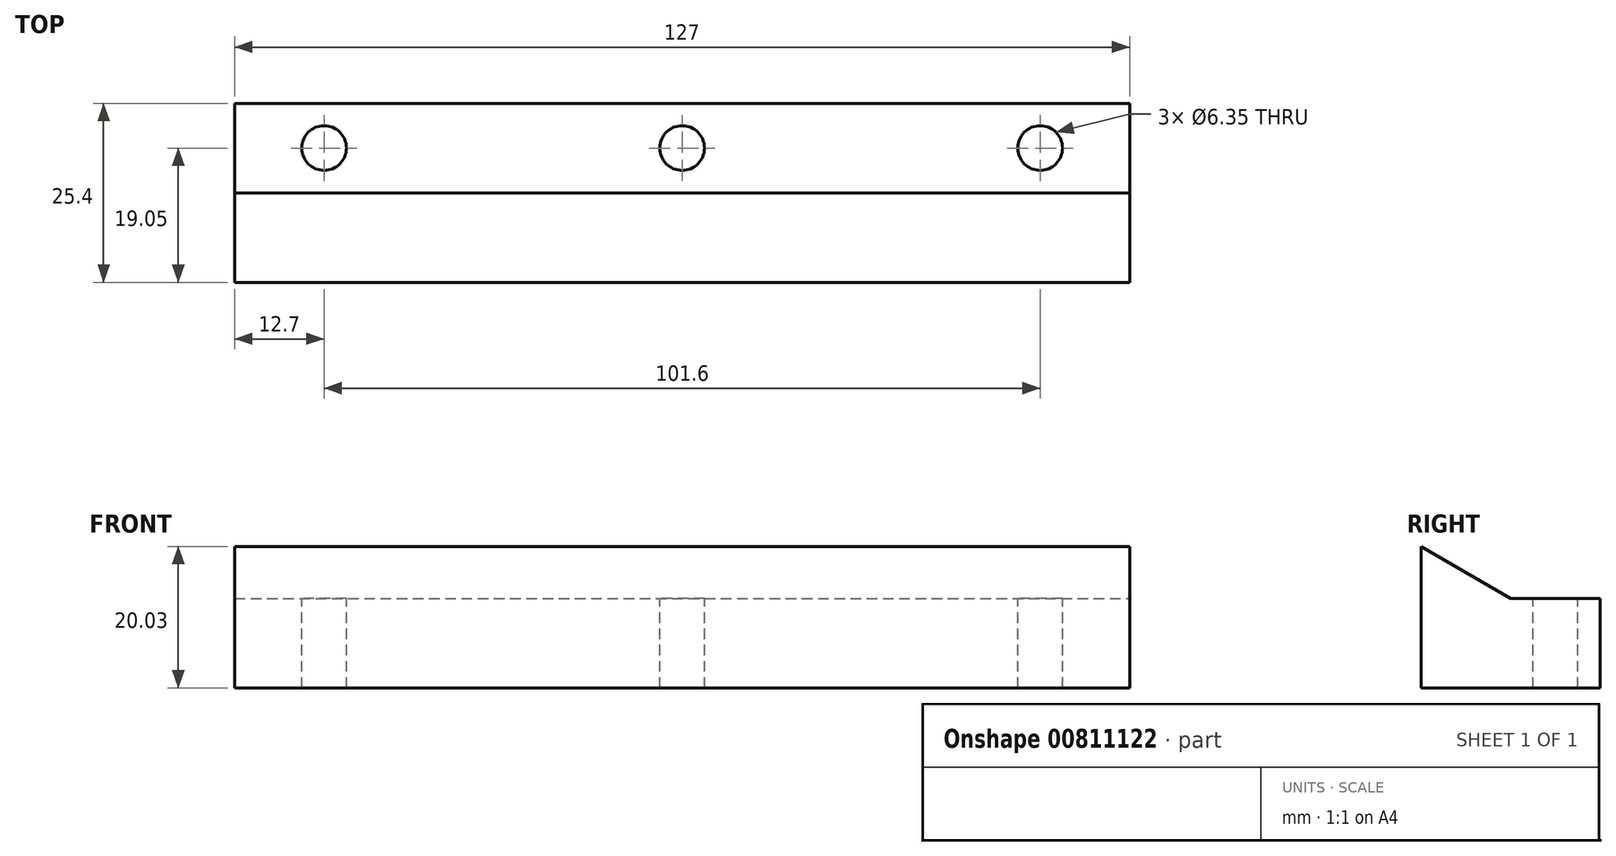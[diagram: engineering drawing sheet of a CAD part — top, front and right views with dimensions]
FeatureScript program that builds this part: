
annotation { "Feature Type Name" : "Feature", "Feature Type Description" : "" }
export const myFeature = defineFeature(function(context is Context, id is Id, definition is map)
    precondition{}
    {
        {
            var Q0;
            Q0=qCreatedBy(makeId("Right.planeOp"),FACE);
            var sketch = newSketch(context, id + "F0", { "sketchPlane" : qUnion([Q0])});
            skLineSegment(sketch, "E0", {"start": v(0, 0) * mm, "end": v(25.4, 0) * mm});
            skLineSegment(sketch, "E1", {"start": v(25.4, 0) * mm, "end": v(25.4, 12.7) * mm});
            skLineSegment(sketch, "E2", {"start": v(25.4, 12.7) * mm, "end": v(12.7, 12.7) * mm});
            skLineSegment(sketch, "E3", {"start": v(12.7, 12.7) * mm, "end": v(0, 20.03) * mm});
            skLineSegment(sketch, "E4", {"start": v(0, 20.03) * mm, "end": v(0, 0) * mm});
            skSolve(sketch);
        }
        {
            var Q0;
            Q0 = qSketchRegion(id + "F0", true);
            extrude(context, id + "F1", {"entities" : qUnion([Q0]), "oppositeDirection" : true, "depth" : 127 * mm, "offsetDistance" : 25.4 * mm});
        }
        {
            var Q0;
            Q0=makeQuery(id+"F1.opExtrude","SWEPT_FACE",FACE,{"disambiguationData":[OSD([sQuery(id+"F0.wireOp",EDGE,"E2")])]});
            var sketch = newSketch(context, id + "F2", { "sketchPlane" : qUnion([Q0])});
            skLineSegment(sketch, "E5", {"start": v(-127, 19.05) * mm, "end": v(0, 19.05) * mm});
            skCircle(sketch, "E6", {"center": v(-63.5, 19.05) * mm, "radius": 3.18 * mm});
            skCircle(sketch, "E7", {"center": v(-12.7, 19.05) * mm, "radius": 3.18 * mm});
            skCircle(sketch, "E8", {"center": v(-114.3, 19.05) * mm, "radius": 3.18 * mm});
            skSolve(sketch);
        }
        {
            var Q0;
            Q0 = qSketchRegion(id + "F2", true);
            extrude(context, id + "F3", {"entities" : qUnion([Q0]), "operationType" : NewBodyOperationType.REMOVE, "endBound" : BoundingType.THROUGH_ALL, "oppositeDirection" : true, "depth" : 25.4 * mm, "offsetDistance" : 25.4 * mm});
        }
    });
